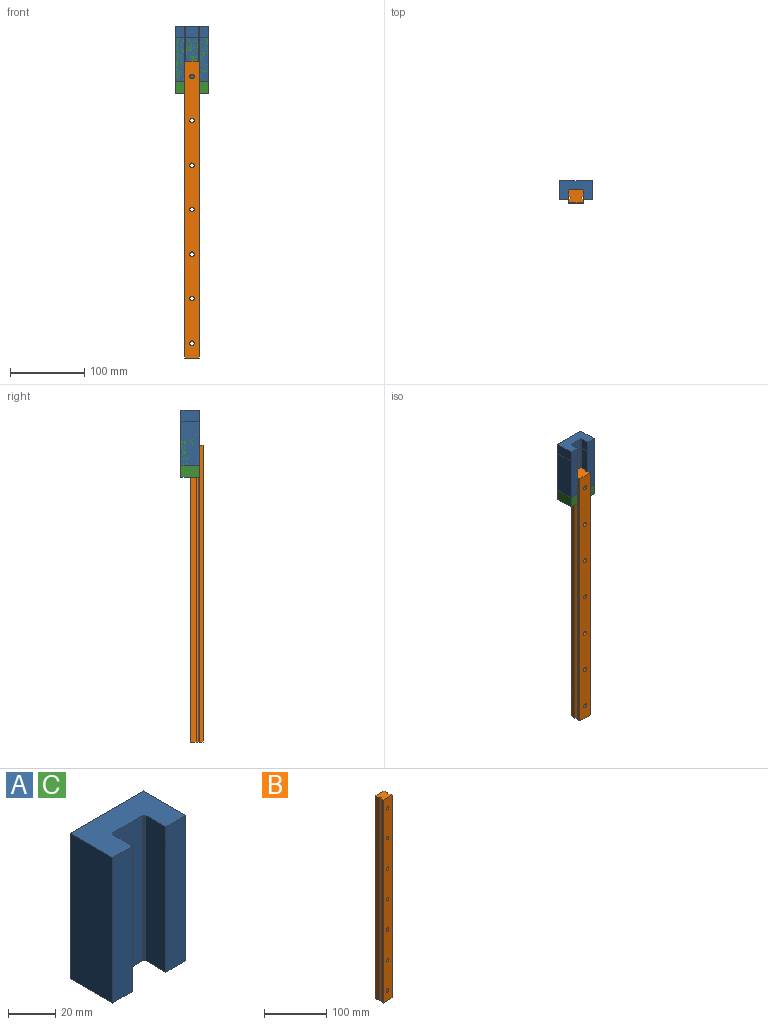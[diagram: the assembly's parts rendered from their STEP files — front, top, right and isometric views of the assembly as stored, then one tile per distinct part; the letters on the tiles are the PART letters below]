
ASSEMBLY  parts=3 mates=4
PART A: 20 faces, bbox 44x25.4x75.5 mm
  f0: plane 75.5x44mm, normal (0,1,0), area 3243.5mm2, adj f1,f9,f10,f11,f12,f14,f16,f18
  f1: plane 75.5x25.4mm, normal (-1,0,0), area 1917.7mm2, adj f0,f2,f10,f11
  f2: plane 75.5x12mm, normal (0,-1,0), area 906mm2, adj f1,f3,f10,f11
  f3: plane 75.5x11.9mm, normal (1,0,0), area 898.4mm2, adj f2,f4,f10,f11
  f4: plane 75.5x1mm, normal (0.71,-0.71,0), area 106.8mm2, adj f3,f5,f10,f11
  f5: plane 75.5x18mm, normal (0,-1,0), area 1359mm2, adj f4,f6,f10,f11
  f6: plane 75.5x1mm, normal (-0.71,-0.71,0), area 106.8mm2, adj f5,f7,f10,f11
  f7: plane 75.5x11.9mm, normal (-1,0,0), area 898.4mm2, adj f6,f8,f10,f11
  f8: plane 75.5x12mm, normal (0,-1,0), area 906mm2, adj f7,f9,f10,f11
  f9: plane 75.5x25.4mm, normal (1,0,0), area 1917.7mm2, adj f0,f8,f10,f11
  f10: plane 44x25.4mm, normal (0,0,1), area 860.6mm2, adj f0,f1,f2,f3,f4,f5,f6,f7
  f11: plane 44x25.4mm, normal (0,0,-1), area 860.6mm2, adj f0,f1,f2,f3,f4,f5,f6,f7
  f12: cylinder r=2.5mm len=5mm, axis (0,1,0), area 78.5mm2, adj f0,f13
  f13: plane 5x5mm, normal (0,1,0), area 19.6mm2, adj f12
  f14: cylinder r=2.5mm len=5mm, axis (0,1,0), area 78.5mm2, adj f0,f15
  f15: plane 5x5mm, normal (0,1,0), area 19.6mm2, adj f14
  f16: cylinder r=2.5mm len=5mm, axis (0,1,0), area 78.5mm2, adj f0,f17
  f17: plane 5x5mm, normal (0,1,0), area 19.6mm2, adj f16
  f18: cylinder r=2.5mm len=5mm, axis (0,1,0), area 78.5mm2, adj f0,f19
  f19: plane 5x5mm, normal (0,1,0), area 19.6mm2, adj f18
PART B: 35 faces, bbox 20x17.5x400 mm
  f0: plane 400x2.5mm, normal (0.72,-0.69,0), area 1387.1mm2, adj f1,f11,f12,f13
  f1: plane 400x6.9mm, normal (1,0,0), area 2760mm2, adj f0,f2,f12,f13
  f2: plane 400x1mm, normal (0.71,0.71,0), area 565.7mm2, adj f1,f3,f12,f13
  f3: plane 400x18mm, normal (0,1,0), area 6703.8mm2, adj f2,f4,f12,f13,f14,f17,f20,f23
  f4: plane 400x1mm, normal (-0.71,0.71,0), area 565.7mm2, adj f3,f5,f12,f13
  f5: plane 400x6.9mm, normal (-1,0,0), area 2760mm2, adj f4,f6,f12,f13
  f6: plane 400x2.5mm, normal (-0.72,-0.69,0), area 1387.1mm2, adj f5,f7,f12,f13
  f7: plane 400x2.5mm, normal (-0.72,0.69,0), area 1387.1mm2, adj f6,f8,f12,f13
  f8: plane 400x4.6mm, normal (-1,0,0), area 1840mm2, adj f7,f9,f12,f13
  f9: plane 400x20mm, normal (0,-1,0), area 7802.1mm2, adj f8,f10,f12,f13,f16,f19,f22,f25
  f10: plane 400x4.6mm, normal (1,0,0), area 1840mm2, adj f9,f11,f12,f13
  f11: plane 400x2.5mm, normal (0.72,0.69,0), area 1387.1mm2, adj f0,f10,f12,f13
  f12: plane 20x17.5mm, normal (0,0,1), area 337mm2, adj f0,f1,f2,f3,f4,f5,f6,f7
  f13: plane 20x17.5mm, normal (0,0,-1), area 337mm2, adj f0,f1,f2,f3,f4,f5,f6,f7
  f14: cylinder r=4.75mm len=9.5mm, axis (0,1,0), area 253.7mm2, adj f3,f15
  f15: plane 9.5x9.5mm, normal (0,1,0), area 42.6mm2, adj f14,f16
  f16: cylinder r=3mm len=9mm, axis (0,1,0), area 169.6mm2, adj f9,f15
  f17: cylinder r=4.75mm len=9.5mm, axis (0,1,0), area 253.7mm2, adj f3,f18
  f18: plane 9.5x9.5mm, normal (0,1,0), area 42.6mm2, adj f17,f19
  f19: cylinder r=3mm len=9mm, axis (0,1,0), area 169.6mm2, adj f9,f18
  f20: cylinder r=4.75mm len=9.5mm, axis (0,1,0), area 253.7mm2, adj f3,f21
  f21: plane 9.5x9.5mm, normal (0,1,0), area 42.6mm2, adj f20,f22
  f22: cylinder r=3mm len=9mm, axis (0,1,0), area 169.6mm2, adj f9,f21
  f23: cylinder r=4.75mm len=9.5mm, axis (0,1,0), area 253.7mm2, adj f3,f24
  f24: plane 9.5x9.5mm, normal (0,1,0), area 42.6mm2, adj f23,f25
  f25: cylinder r=3mm len=9mm, axis (0,1,0), area 169.6mm2, adj f9,f24
  f26: cylinder r=4.75mm len=9.5mm, axis (0,1,0), area 253.7mm2, adj f3,f27
  f27: plane 9.5x9.5mm, normal (0,1,0), area 42.6mm2, adj f26,f28
  f28: cylinder r=3mm len=9mm, axis (0,1,0), area 169.6mm2, adj f9,f27
  f29: cylinder r=4.75mm len=9.5mm, axis (0,1,0), area 253.7mm2, adj f3,f30
  f30: plane 9.5x9.5mm, normal (0,1,0), area 42.6mm2, adj f29,f31
  f31: cylinder r=3mm len=9mm, axis (0,1,0), area 169.6mm2, adj f9,f30
  f32: cylinder r=4.75mm len=9.5mm, axis (0,1,0), area 253.7mm2, adj f3,f33
  f33: plane 9.5x9.5mm, normal (0,1,0), area 42.6mm2, adj f32,f34
  f34: cylinder r=3mm len=9mm, axis (0,1,0), area 169.6mm2, adj f9,f33
PART C: same geometry as A
PLACE A t=(-99.15,147.51,372.25)mm
PLACE B at identity
PLACE C t=(-99.15,147.51,356.95)mm
MATE planar C.f5 <-> B.f17  axis (0,-1,0) through (-7.08,30.61,394.7)mm
MATE planar C.f3 <-> B.f5  axis (1,0,0) through (-17.08,23.66,394.7)mm
MATE planar A.f5 <-> B.f17  axis (0,-1,0) through (-7.08,30.61,410)mm
MATE planar A.f3 <-> B.f5  axis (1,0,0) through (-17.08,23.66,410)mm
